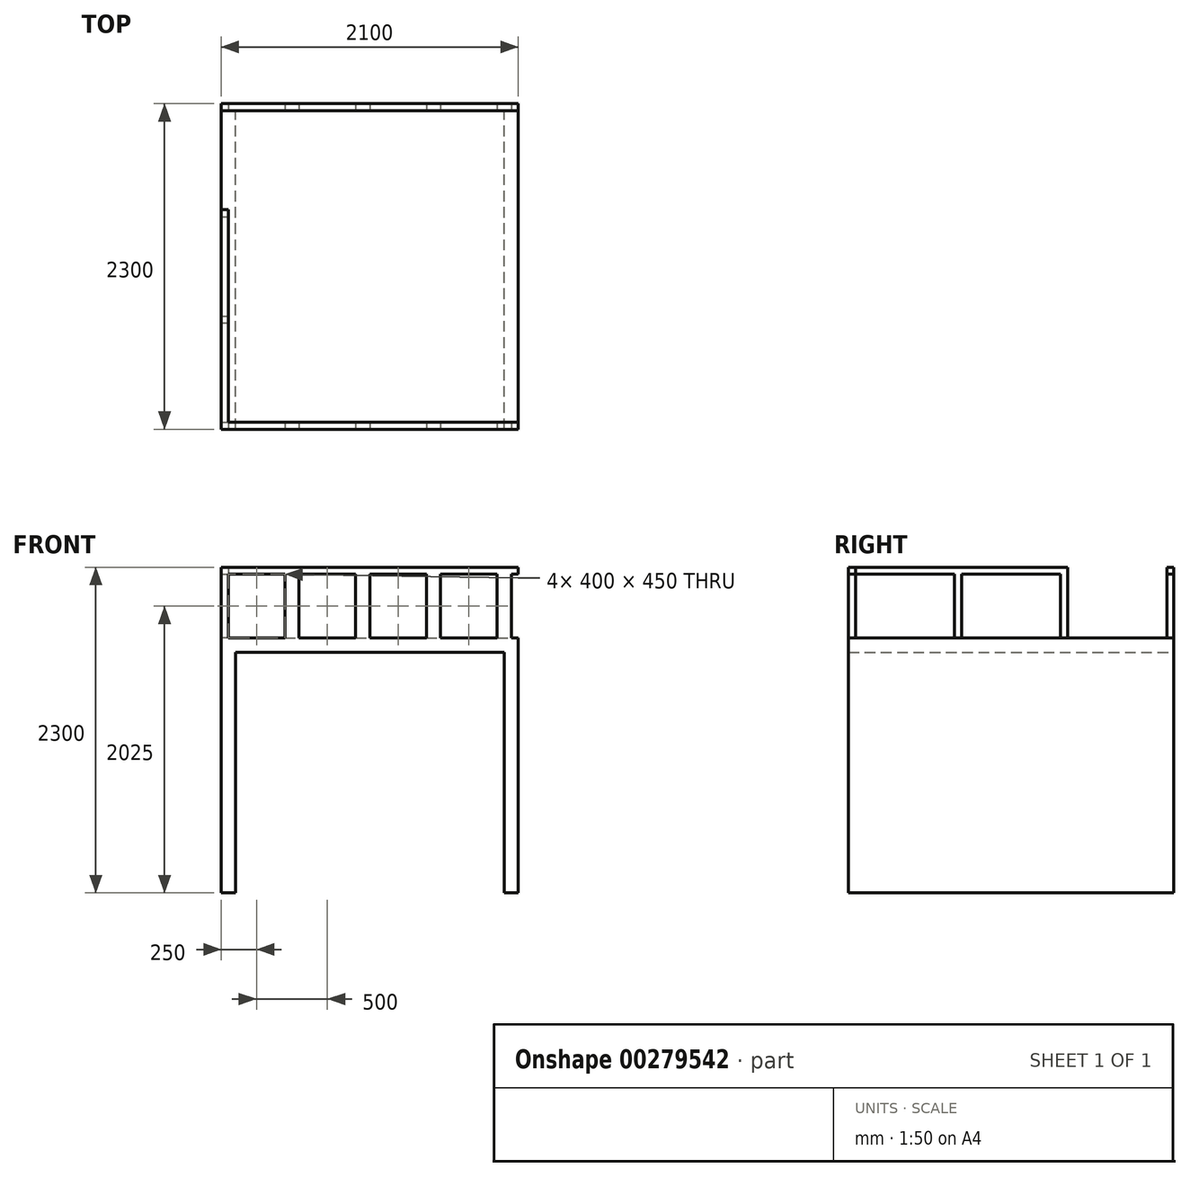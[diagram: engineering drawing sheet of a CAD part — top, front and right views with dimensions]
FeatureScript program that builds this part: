
annotation { "Feature Type Name" : "Feature", "Feature Type Description" : "" }
export const myFeature = defineFeature(function(context is Context, id is Id, definition is map)
    precondition{}
    {
        {
            var Q0;
            Q0=qCreatedBy(makeId("Front.planeOp"),FACE);
            var sketch = newSketch(context, id + "F0", { "sketchPlane" : qUnion([Q0])});
            skLineSegment(sketch, "E0", {"start": v(-1050, 0) * mm, "end": v(-1050, 1800) * mm});
            skLineSegment(sketch, "E1", {"start": v(-1050, 1800) * mm, "end": v(0, 1800) * mm});
            skLineSegment(sketch, "E2", {"start": v(0, 1800) * mm, "end": v(0, -22.44) * mm, "construction": true});
            skLineSegment(sketch, "E3", {"start": v(0, 1800) * mm, "end": v(0, 1700) * mm});
            skLineSegment(sketch, "E4", {"start": v(0, 1700) * mm, "end": v(-950, 1700) * mm});
            skLineSegment(sketch, "E5", {"start": v(-950, 1700) * mm, "end": v(-950, 0) * mm});
            skLineSegment(sketch, "E6", {"start": v(-950, 0) * mm, "end": v(-1050, 0) * mm});
            skSolve(sketch);
        }
        {
            var Q0;
            Q0 = qSketchRegion(id + "F0", true);
            extrude(context, id + "F1", {"entities" : qUnion([Q0]), "depth" : 2300 * mm});
        }
        {
            var Q0;
            Q0=makeQuery(id+"F1.opExtrude","SWEPT_BODY",BODY,{"disambiguationData":[OSD([sQuery(id+"F0.wireOp",EDGE,"E0"),sQuery(id+"F0.wireOp",EDGE,"E1"),sQuery(id+"F0.wireOp",EDGE,"E3"),sQuery(id+"F0.wireOp",EDGE,"E4"),sQuery(id+"F0.wireOp",EDGE,"E5"),sQuery(id+"F0.wireOp",EDGE,"E6")])]});
            var Q1;
            Q1=qCreatedBy(makeId("Right.planeOp"),FACE);
            mirror(context, id + "F2", {"operationType" : NewBodyOperationType.ADD, "entities" : qUnion([Q0]), "mirrorPlane" : qUnion([Q1])});
        }
        {
            var Q0;
            {var subQ0=makeQuery(id+"F1.opExtrude","SWEPT_FACE",FACE,{"disambiguationData":[OSD([sQuery(id+"F0.wireOp",EDGE,"E1")])]});Q0=makeQuery(id+"F2.boolean.opBoolean","MERGE",FACE,{"derivedFrom":[subQ0,makeQuery(id+"F2.opPattern","COPY",FACE,{"derivedFrom":subQ0,"instanceName":"1"})]});}
            var sketch = newSketch(context, id + "F3", { "sketchPlane" : qUnion([Q0])});
            skLineSegment(sketch, "E7.bottom", {"start": v(1050, -2300) * mm, "end": v(-1050, -2300) * mm});
            skLineSegment(sketch, "E7.top", {"start": v(1050, 0) * mm, "end": v(-1050, 0) * mm});
            skLineSegment(sketch, "E7.left", {"start": v(1050, -2300) * mm, "end": v(1050, -2250) * mm});
            skLineSegment(sketch, "E7.right", {"start": v(-1050, -2300) * mm, "end": v(-1050, -750) * mm});
            skLineSegment(sketch, "E8", {"start": v(1050, -50) * mm, "end": v(-1000, -50) * mm});
            skLineSegment(sketch, "E9", {"start": v(-1000, -750) * mm, "end": v(-1000, -2250) * mm});
            skLineSegment(sketch, "E10", {"start": v(-1000, -2250) * mm, "end": v(1050, -2250) * mm});
            skLineSegment(sketch, "E11", {"start": v(-1000, -750) * mm, "end": v(-1050, -750) * mm});
            skLineSegment(sketch, "E12", {"start": v(-1000, -50) * mm, "end": v(-1050, -50) * mm});
            skLineSegment(sketch, "E13.trimOffspring", {"start": v(-1050, -50) * mm, "end": v(-1050, 0) * mm});
            skLineSegment(sketch, "E14.trimOffspring", {"start": v(1050, -50) * mm, "end": v(1050, 0) * mm});
            skSolve(sketch);
        }
        {
            var Q0;
            Q0 = qSketchRegion(id + "F3", true);
            extrude(context, id + "F4", {"entities" : qUnion([Q0]), "operationType" : NewBodyOperationType.ADD, "depth" : 500 * mm});
        }
        {
            var Q0;
            {var subQ0=makeQuery(id+"F1.opExtrude","CAP_FACE",FACE,{"disambiguationData":[OSD([sQuery(id+"F0.wireOp",EDGE,"E0"),sQuery(id+"F0.wireOp",EDGE,"E1"),sQuery(id+"F0.wireOp",EDGE,"E3"),sQuery(id+"F0.wireOp",EDGE,"E4"),sQuery(id+"F0.wireOp",EDGE,"E5"),sQuery(id+"F0.wireOp",EDGE,"E6")])],"isStart":false});Q0=makeQuery(id+"F4.boolean.opBoolean","MERGE",FACE,{"derivedFrom":[makeQuery(id+"F2.boolean.opBoolean","MERGE",FACE,{"derivedFrom":[subQ0,makeQuery(id+"F2.opPattern","COPY",FACE,{"derivedFrom":subQ0,"instanceName":"1"})]}),makeQuery(id+"F4.opExtrude","SWEPT_FACE",FACE,{"disambiguationData":[OSD([sQuery(id+"F3.wireOp",EDGE,"E7.bottom")])]})]});}
            var sketch = newSketch(context, id + "F5", { "sketchPlane" : qUnion([Q0])});
            skLineSegment(sketch, "E15.bottom", {"start": v(-1000, 2250) * mm, "end": v(-600, 2250) * mm});
            skLineSegment(sketch, "E15.top", {"start": v(-1000, 1800) * mm, "end": v(-600, 1800) * mm});
            skLineSegment(sketch, "E15.left", {"start": v(-1000, 2250) * mm, "end": v(-1000, 1800) * mm});
            skLineSegment(sketch, "E15.right", {"start": v(-600, 2250) * mm, "end": v(-600, 1800) * mm});
            skLineSegment(sketch, "E16.1.0.0", {"start": v(-500, 2250) * mm, "end": v(-500, 1800) * mm});
            skLineSegment(sketch, "E16.1.0.1", {"start": v(-500, 2250) * mm, "end": v(-100, 2250) * mm});
            skLineSegment(sketch, "E16.1.0.2", {"start": v(-100, 2250) * mm, "end": v(-100, 1800) * mm});
            skLineSegment(sketch, "E16.1.0.3", {"start": v(-500, 1800) * mm, "end": v(-100, 1800) * mm});
            skLineSegment(sketch, "E16.2.0.0", {"start": v(0, 2250) * mm, "end": v(0, 1800) * mm});
            skLineSegment(sketch, "E16.2.0.1", {"start": v(0, 2250) * mm, "end": v(400, 2250) * mm});
            skLineSegment(sketch, "E16.2.0.2", {"start": v(400, 2250) * mm, "end": v(400, 1800) * mm});
            skLineSegment(sketch, "E16.2.0.3", {"start": v(0, 1800) * mm, "end": v(400, 1800) * mm});
            skLineSegment(sketch, "E16.direction1", {"start": v(-1000, 1800) * mm, "end": v(-500, 1800) * mm, "construction": true});
            skLineSegment(sketch, "E17.0.3.0", {"start": v(500, 2250) * mm, "end": v(500, 1800) * mm});
            skLineSegment(sketch, "E17.3.3.0", {"start": v(500, 2250) * mm, "end": v(900, 2250) * mm});
            skLineSegment(sketch, "E17.6.3.0", {"start": v(900, 2250) * mm, "end": v(900, 1800) * mm});
            skLineSegment(sketch, "E17.9.3.0", {"start": v(500, 1800) * mm, "end": v(900, 1800) * mm});
            skLineSegment(sketch, "E18.0.4.0", {"start": v(1000, 2250) * mm, "end": v(1000, 1800) * mm});
            skLineSegment(sketch, "E18.3.4.0", {"start": v(1000, 2250) * mm, "end": v(1400, 2250) * mm});
            skLineSegment(sketch, "E18.6.4.0", {"start": v(1400, 2250) * mm, "end": v(1400, 1800) * mm});
            skLineSegment(sketch, "E18.9.4.0", {"start": v(1000, 1800) * mm, "end": v(1400, 1800) * mm});
            skSolve(sketch);
        }
        {
            var Q0;
            Q0 = qSketchRegion(id + "F5", true);
            extrude(context, id + "F6", {"entities" : qUnion([Q0]), "operationType" : NewBodyOperationType.REMOVE, "endBound" : BoundingType.THROUGH_ALL, "oppositeDirection" : true, "depth" : 25 * mm});
        }
        {
            var Q0;
            Q0=makeQuery(id+"F6.boolean.opBoolean","MERGE",FACE,{"derivedFrom":[makeQuery(id+"F4.opExtrude","SWEPT_FACE",FACE,{"disambiguationData":[OSD([sQuery(id+"F3.wireOp",EDGE,"E9")])]}),makeQuery(id+"F6.opExtrude","SWEPT_FACE",FACE,{"disambiguationData":[OSD([sQuery(id+"F5.wireOp",EDGE,"E15.left")])]})]});
            var sketch = newSketch(context, id + "F7", { "sketchPlane" : qUnion([Q0])});
            skLineSegment(sketch, "E19.bottom", {"start": v(-2250, 2250) * mm, "end": v(-1550, 2250) * mm});
            skLineSegment(sketch, "E19.top", {"start": v(-2250, 1800) * mm, "end": v(-1550, 1800) * mm});
            skLineSegment(sketch, "E19.left", {"start": v(-2250, 2250) * mm, "end": v(-2250, 1800) * mm});
            skLineSegment(sketch, "E19.right", {"start": v(-1550, 2250) * mm, "end": v(-1550, 1800) * mm});
            skLineSegment(sketch, "E20.1.0.0", {"start": v(-1500, 2250) * mm, "end": v(-1500, 1800) * mm});
            skLineSegment(sketch, "E20.1.0.1", {"start": v(-1500, 2250) * mm, "end": v(-800, 2250) * mm});
            skLineSegment(sketch, "E20.1.0.2", {"start": v(-800, 2250) * mm, "end": v(-800, 1800) * mm});
            skLineSegment(sketch, "E20.1.0.3", {"start": v(-1500, 1800) * mm, "end": v(-800, 1800) * mm});
            skLineSegment(sketch, "E20.direction1", {"start": v(-2250, 1800) * mm, "end": v(-1500, 1800) * mm, "construction": true});
            skSolve(sketch);
        }
        {
            var Q0;
            Q0 = qSketchRegion(id + "F7", true);
            extrude(context, id + "F8", {"entities" : qUnion([Q0]), "operationType" : NewBodyOperationType.REMOVE, "endBound" : BoundingType.UP_TO_NEXT, "oppositeDirection" : true, "depth" : 25 * mm});
        }
    });
